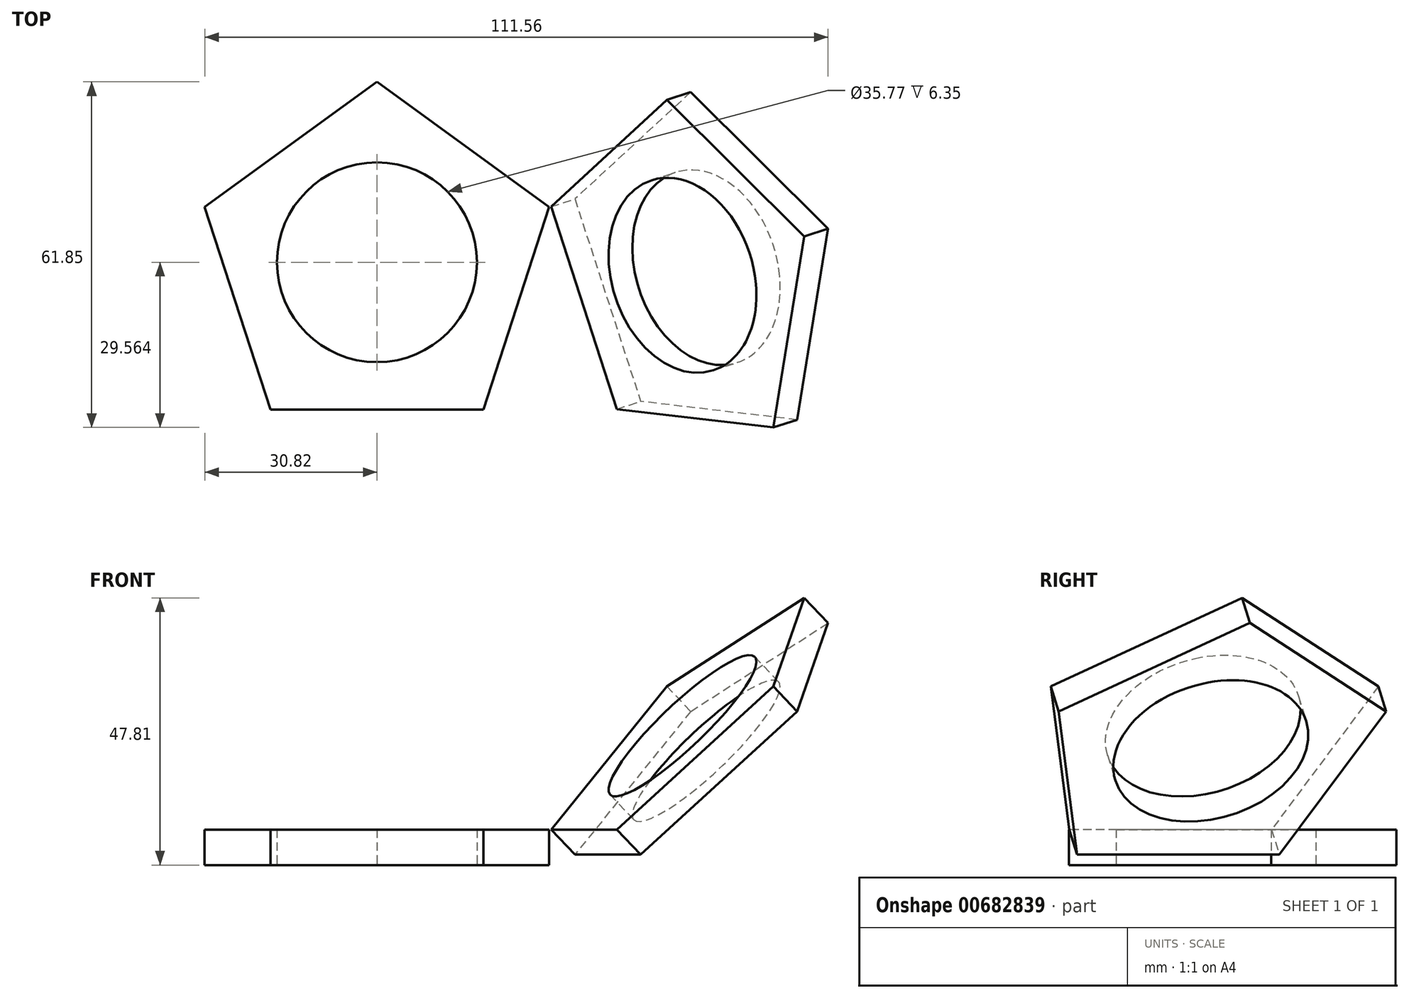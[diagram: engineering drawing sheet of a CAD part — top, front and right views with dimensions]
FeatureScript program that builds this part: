
annotation { "Feature Type Name" : "Feature", "Feature Type Description" : "" }
export const myFeature = defineFeature(function(context is Context, id is Id, definition is map)
    precondition{}
    {
        {
            var Q0;
            Q0=qCreatedBy(makeId("Top.planeOp"),FACE);
            var sketch = newSketch(context, id + "F0", { "sketchPlane" : qUnion([Q0])});
            skLineSegment(sketch, "E0", {"start": v(0, 56.21) * mm, "end": v(-30.82, 33.82) * mm});
            skLineSegment(sketch, "E1", {"start": v(0, 56.21) * mm, "end": v(30.82, 33.82) * mm});
            skLineSegment(sketch, "E2", {"start": v(30.82, 33.82) * mm, "end": v(19.05, -2.42) * mm});
            skLineSegment(sketch, "E3", {"start": v(19.05, -2.42) * mm, "end": v(-19.05, -2.42) * mm});
            skLineSegment(sketch, "E4", {"start": v(-30.82, 33.82) * mm, "end": v(-19.05, -2.42) * mm});
            skCircle(sketch, "E5", {"center": v(0, 23.92) * mm, "radius": 17.88 * mm});
            skSolve(sketch);
        }
        {
            var Q0;
            Q0 = qSketchRegion(id + "F0", true);
            extrude(context, id + "F1", {"entities" : qUnion([Q0]), "depth" : 6.35 * mm, "offsetDistance" : 25.4 * mm});
        }
        {
            var Q0;
            Q0=qCreatedBy(makeId("Top.planeOp"),FACE);
            var sketch = newSketch(context, id + "F2", { "sketchPlane" : qUnion([Q0])});
            skLineSegment(sketch, "E6", {"start": v(0, 32.39) * mm, "end": v(-30.82, 10) * mm});
            skLineSegment(sketch, "E7", {"start": v(0, 32.39) * mm, "end": v(30.82, 10) * mm});
            skLineSegment(sketch, "E8", {"start": v(30.82, 10) * mm, "end": v(19.05, -26.24) * mm});
            skLineSegment(sketch, "E9", {"start": v(19.05, -26.24) * mm, "end": v(-19.05, -26.24) * mm});
            skLineSegment(sketch, "E10", {"start": v(-30.82, 10) * mm, "end": v(-19.05, -26.24) * mm});
            skCircle(sketch, "E11", {"center": v(0, 0.1) * mm, "radius": 17.88 * mm});
            skSolve(sketch);
        }
        {
            var Q0;
            Q0 = qSketchRegion(id + "F2", true);
            extrude(context, id + "F3", {"entities" : qUnion([Q0]), "depth" : 6.35 * mm, "offsetDistance" : 25.4 * mm});
        }
        {
            var Q0;
            Q0=makeQuery(id+"F3.opExtrude","SWEPT_BODY",BODY,{"disambiguationData":[OSD([sQuery(id+"F2.wireOp",EDGE,"E6"),sQuery(id+"F2.wireOp",EDGE,"E7"),sQuery(id+"F2.wireOp",EDGE,"E8"),sQuery(id+"F2.wireOp",EDGE,"E9"),sQuery(id+"F2.wireOp",EDGE,"E10"),sQuery(id+"F2.wireOp",EDGE,"E11")])]});
            var Q1;
            Q1=makeQuery(id+"F1.opExtrude","CAP_EDGE",EDGE,{"disambiguationData":[OSD([sQuery(id+"F0.wireOp",EDGE,"E4")])],"isStart":false});
            transform(context, id + "F4", {"entities" : qUnion([Q0]), "transformType" : TransformType.TRANSLATION_3D, "dx" : 61.98 * mm, "dy" : 23.88 * mm, "dz" : 0 * mm, "makeCopy" : false});
        }
        {
            var Q0;
            Q0=makeQuery(id+"F3.opExtrude","SWEPT_BODY",BODY,{"disambiguationData":[OSD([sQuery(id+"F2.wireOp",EDGE,"E6"),sQuery(id+"F2.wireOp",EDGE,"E7"),sQuery(id+"F2.wireOp",EDGE,"E8"),sQuery(id+"F2.wireOp",EDGE,"E9"),sQuery(id+"F2.wireOp",EDGE,"E10"),sQuery(id+"F2.wireOp",EDGE,"E11")])]});
            var Q1;
            Q1=makeQuery(id+"F3.opExtrude","CAP_EDGE",EDGE,{"disambiguationData":[OSD([sQuery(id+"F2.wireOp",EDGE,"E10")])],"isStart":false});
            transform(context, id + "F5", {"entities" : qUnion([Q0]), "transformType" : TransformType.ROTATION, "transformAxis" : qUnion([Q1]), "angle" : 45 * degree, "makeCopy" : false});
        }
    });
